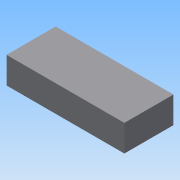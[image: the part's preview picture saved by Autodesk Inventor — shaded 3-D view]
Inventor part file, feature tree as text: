
AUTODESK INVENTOR PART (.ipt)
format: ipt  version: 2015 (Build 190159000, 159)  size: 68,096 bytes
history: native  units: in
note: dims shown in document units (in); Inventor stores cm internally (conversion verified against a paired STEP export)
features: extrude x1, sketch x1
ambient origin geometry x8: Origin, YZ Plane, XZ Plane, XY Plane, X Axis, Y Axis, Z Axis, Center Point
bodies: Solid1 (feature_tree)
feature tree (2):
  extrude  "Extrusion1"  Depth=1.063in
  sketch  "Sketch1"  dims[d0=4.7244in d1=1.063in d2=1.9685in d3=0.0in]
